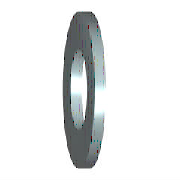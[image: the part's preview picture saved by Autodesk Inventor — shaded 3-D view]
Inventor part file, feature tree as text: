
AUTODESK INVENTOR PART (.ipt)
format: ipt  version: 2025.2 (Build 292293000, 293)  size: 104,960 bytes
history: native  units: mm (DEFAULTED — no unit token found)
features: extrude x1, other x1, plane x1
ambient origin geometry x7: Origin, YZ Plane, XY Plane, X Axis, Y Axis, Z Axis, Center Point
bodies: Solid1 (feature_tree)
feature tree (3):
  extrude  "Körper"  Depth=15.5mm
  other  "Work Axis1"
  plane  "Work Plane1"
